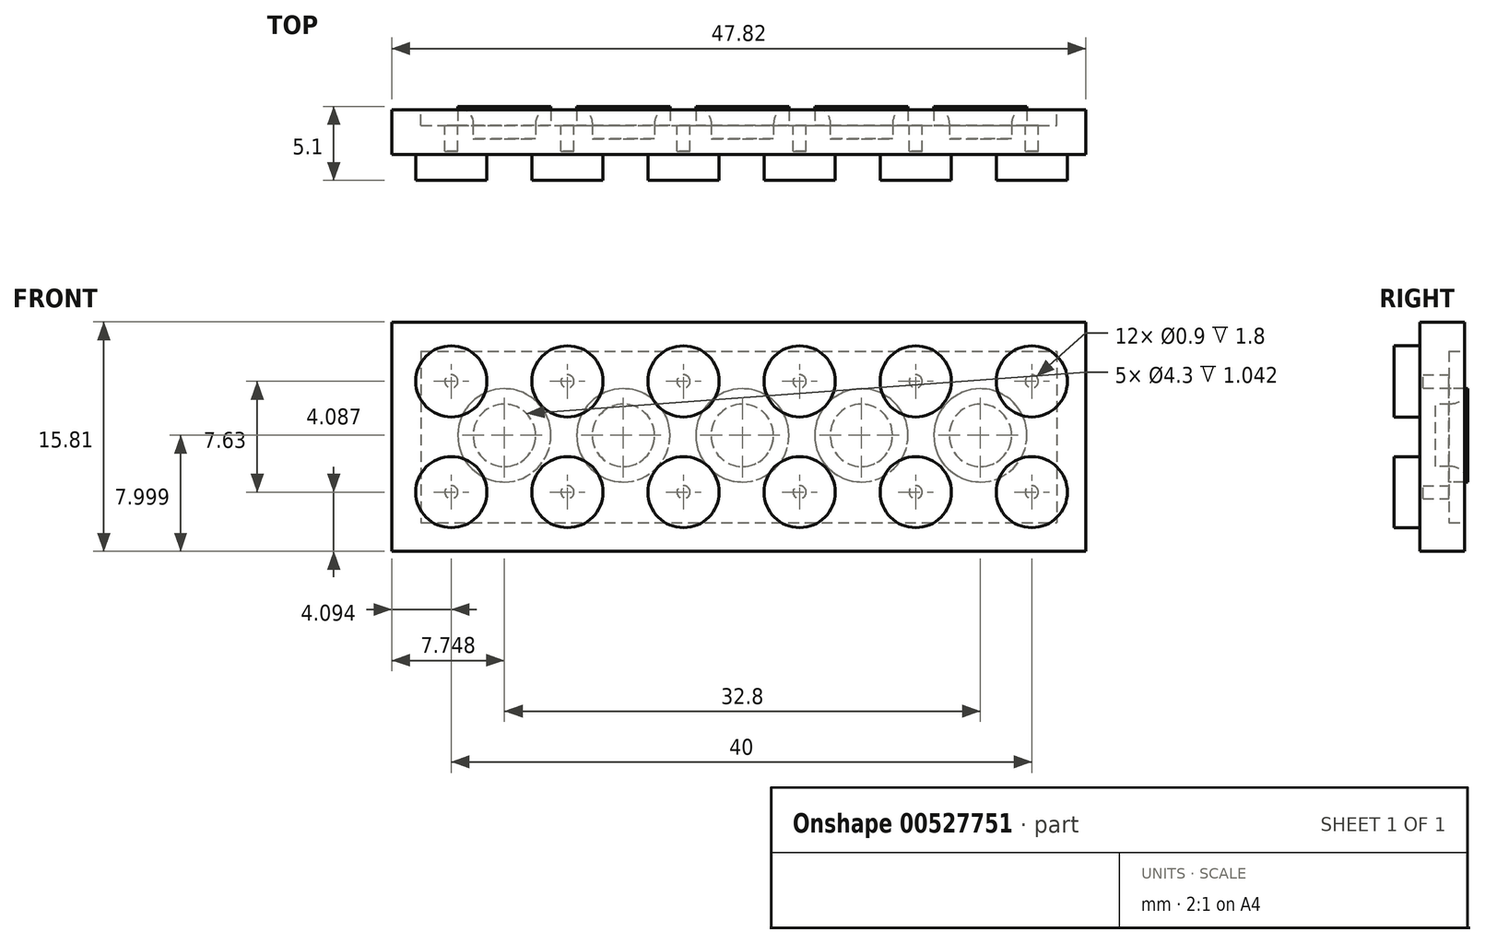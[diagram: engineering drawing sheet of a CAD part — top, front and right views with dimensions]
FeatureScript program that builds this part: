
annotation { "Feature Type Name" : "Feature", "Feature Type Description" : "" }
export const myFeature = defineFeature(function(context is Context, id is Id, definition is map)
    precondition{}
    {
        {
            var Q0;
            Q0=qCreatedBy(makeId("Front.planeOp"),FACE);
            var sketch = newSketch(context, id + "F0", { "sketchPlane" : qUnion([Q0])});
            skLineSegment(sketch, "E0.bottom", {"start": v(-37.29, 28.54) * mm, "end": v(10.53, 28.54) * mm});
            skLineSegment(sketch, "E0.top", {"start": v(-37.29, 12.73) * mm, "end": v(10.53, 12.73) * mm});
            skLineSegment(sketch, "E0.left", {"start": v(-37.29, 28.54) * mm, "end": v(-37.29, 12.73) * mm});
            skLineSegment(sketch, "E0.right", {"start": v(10.53, 28.54) * mm, "end": v(10.53, 12.73) * mm});
            skSolve(sketch);
        }
        {
            var Q0;
            Q0=makeQuery(id+"F0.imprint","IMPRINT",FACE,{"disambiguationData":[TD([[makeQuery(id+"F0.imprint","IMPRINT",EDGE,{"derivedFrom":sQuery(id+"F0.wireOp",EDGE,"E0.bottom")}),-1.0]])]});
            extrude(context, id + "F1", {"entities" : qUnion([Q0]), "depth" : 3.06 * mm, "offsetDistance" : 25 * mm});
        }
        {
            var Q0;
            Q0=makeQuery(id+"F1.opExtrude","CAP_FACE",FACE,{"disambiguationData":[OSD([sQuery(id+"F0.wireOp",EDGE,"E0.bottom"),sQuery(id+"F0.wireOp",EDGE,"E0.top"),sQuery(id+"F0.wireOp",EDGE,"E0.left"),sQuery(id+"F0.wireOp",EDGE,"E0.right")])],"isStart":false});
            var sketch = newSketch(context, id + "F2", { "sketchPlane" : qUnion([Q0])});
            skCircle(sketch, "E1", {"center": v(-33.2, 24.45) * mm, "radius": 2.45 * mm});
            skCircle(sketch, "E2", {"center": v(-33.2, 16.82) * mm, "radius": 2.45 * mm});
            skCircle(sketch, "E3.1.0.0", {"center": v(-25.2, 16.82) * mm, "radius": 2.45 * mm});
            skCircle(sketch, "E3.1.0.1", {"center": v(-25.2, 24.45) * mm, "radius": 2.45 * mm});
            skCircle(sketch, "E3.2.0.0", {"center": v(-17.2, 16.82) * mm, "radius": 2.45 * mm});
            skCircle(sketch, "E3.2.0.1", {"center": v(-17.2, 24.45) * mm, "radius": 2.45 * mm});
            skCircle(sketch, "E3.3.0.0", {"center": v(-9.2, 16.82) * mm, "radius": 2.45 * mm});
            skCircle(sketch, "E3.3.0.1", {"center": v(-9.2, 24.45) * mm, "radius": 2.45 * mm});
            skCircle(sketch, "E3.4.0.0", {"center": v(-1.2, 16.82) * mm, "radius": 2.45 * mm});
            skCircle(sketch, "E3.4.0.1", {"center": v(-1.2, 24.45) * mm, "radius": 2.45 * mm});
            skCircle(sketch, "E3.5.0.0", {"center": v(6.8, 16.82) * mm, "radius": 2.45 * mm});
            skCircle(sketch, "E3.5.0.1", {"center": v(6.8, 24.45) * mm, "radius": 2.45 * mm});
            skLineSegment(sketch, "E3.direction1", {"start": v(-33.2, 16.82) * mm, "end": v(-25.2, 16.82) * mm, "construction": true});
            skSolve(sketch);
        }
        {
            var Q0;
            Q0 = qSketchRegion(id + "F2", true);
            extrude(context, id + "F3", {"entities" : qUnion([Q0]), "operationType" : NewBodyOperationType.ADD, "depth" : 1.8 * mm, "offsetDistance" : 25 * mm});
        }
        {
            var Q0;
            Q0=makeQuery(id+"F1.opExtrude","CAP_FACE",FACE,{"disambiguationData":[OSD([sQuery(id+"F0.wireOp",EDGE,"E0.bottom"),sQuery(id+"F0.wireOp",EDGE,"E0.top"),sQuery(id+"F0.wireOp",EDGE,"E0.left"),sQuery(id+"F0.wireOp",EDGE,"E0.right")])],"isStart":true});
            shell(context, id + "F4", {"entities" : qUnion([Q0]), "thickness" : 2 * mm});
        }
        {
            var Q0;
            Q0=makeQuery(id+"F4.opShell","OFFSET_FACE",FACE,{"disambiguationData":[OSD([sQuery(id+"F0.wireOp",EDGE,"E0.bottom"),sQuery(id+"F0.wireOp",EDGE,"E0.top"),sQuery(id+"F0.wireOp",EDGE,"E0.left"),sQuery(id+"F0.wireOp",EDGE,"E0.right")])]});
            var sketch = newSketch(context, id + "F5", { "sketchPlane" : qUnion([Q0])});
            skCircle(sketch, "E4", {"center": v(29.54, 20.73) * mm, "radius": 3.2 * mm});
            skCircle(sketch, "E5.1.0.0", {"center": v(21.34, 20.73) * mm, "radius": 3.2 * mm});
            skCircle(sketch, "E5.2.0.0", {"center": v(13.14, 20.73) * mm, "radius": 3.2 * mm});
            skCircle(sketch, "E5.3.0.0", {"center": v(4.94, 20.73) * mm, "radius": 3.2 * mm});
            skCircle(sketch, "E5.4.0.0", {"center": v(-3.26, 20.73) * mm, "radius": 3.2 * mm});
            skLineSegment(sketch, "E5.direction1", {"start": v(29.54, 20.73) * mm, "end": v(21.34, 20.73) * mm, "construction": true});
            skSolve(sketch);
        }
        {
            var Q0;
            Q0 = qSketchRegion(id + "F5", true);
            extrude(context, id + "F6", {"entities" : qUnion([Q0]), "operationType" : NewBodyOperationType.ADD, "depth" : 1.3 * mm, "offsetDistance" : 25 * mm});
        }
        {
            var Q0;
            Q0=makeQuery(id+"F6.opExtrude","CAP_FACE",FACE,{"disambiguationData":[OSD([sQuery(id+"F5.wireOp",EDGE,"E5.4.0.0")])],"isStart":false});
            var Q1;
            Q1=makeQuery(id+"F6.opExtrude","CAP_FACE",FACE,{"disambiguationData":[OSD([sQuery(id+"F5.wireOp",EDGE,"E5.3.0.0")])],"isStart":false});
            var Q2;
            Q2=makeQuery(id+"F6.opExtrude","CAP_FACE",FACE,{"disambiguationData":[OSD([sQuery(id+"F5.wireOp",EDGE,"E5.2.0.0")])],"isStart":false});
            var Q3;
            Q3=makeQuery(id+"F6.opExtrude","CAP_FACE",FACE,{"disambiguationData":[OSD([sQuery(id+"F5.wireOp",EDGE,"E5.1.0.0")])],"isStart":false});
            var Q4;
            Q4=makeQuery(id+"F6.opExtrude","CAP_FACE",FACE,{"disambiguationData":[OSD([sQuery(id+"F5.wireOp",EDGE,"E4")])],"isStart":false});
            shell(context, id + "F7", {"entities" : qUnion([Q0, Q1, Q2, Q3, Q4]), "thickness" : 1.06 * mm});
        }
        {
            var Q0;
            Q0=makeQuery(id+"F7.opShell","OFFSET_EDGE",EDGE,{"disambiguationData":[OSD([sQuery(id+"F5.wireOp",EDGE,"E5.4.0.0")])]});
            var Q1;
            Q1=makeQuery(id+"F7.opShell","OFFSET_EDGE",EDGE,{"disambiguationData":[OSD([sQuery(id+"F5.wireOp",EDGE,"E5.3.0.0")])]});
            var Q2;
            Q2=makeQuery(id+"F7.opShell","OFFSET_EDGE",EDGE,{"disambiguationData":[OSD([sQuery(id+"F5.wireOp",EDGE,"E5.2.0.0")])]});
            var Q3;
            Q3=makeQuery(id+"F7.opShell","OFFSET_EDGE",EDGE,{"disambiguationData":[OSD([sQuery(id+"F5.wireOp",EDGE,"E5.1.0.0")])]});
            var Q4;
            Q4=makeQuery(id+"F7.opShell","OFFSET_EDGE",EDGE,{"disambiguationData":[OSD([sQuery(id+"F5.wireOp",EDGE,"E4")])]});
            fillet(context, id + "F8", {"entities" : qUnion([Q0, Q1, Q2, Q3, Q4]), "radius" : 1.2 * mm, "tangentPropagation" : true, "allowEdgeOverflow" : false});
        }
    });
